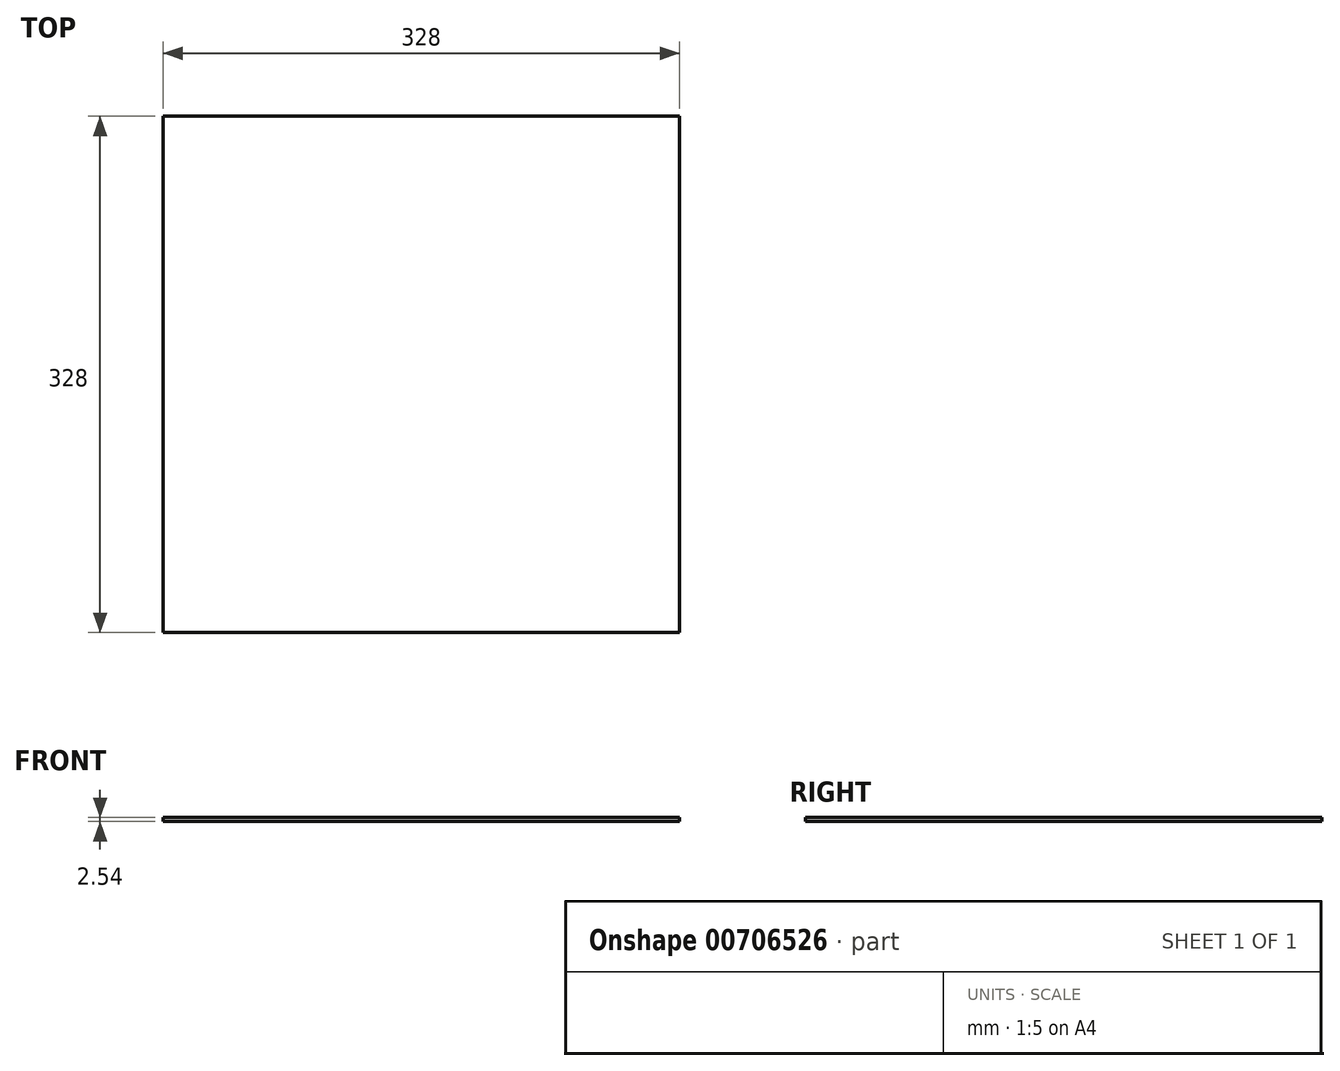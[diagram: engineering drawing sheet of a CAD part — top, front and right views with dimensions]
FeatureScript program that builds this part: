
annotation { "Feature Type Name" : "Feature", "Feature Type Description" : "" }
export const myFeature = defineFeature(function(context is Context, id is Id, definition is map)
    precondition{}
    {
        {
            var Q0;
            Q0=qCreatedBy(makeId("Top.planeOp"),FACE);
            var sketch = newSketch(context, id + "F0", { "sketchPlane" : qUnion([Q0])});
            skLineSegment(sketch, "E0.bottom", {"start": v(0, 0) * mm, "end": v(-328, 0) * mm});
            skLineSegment(sketch, "E0.top", {"start": v(0, -328) * mm, "end": v(-328, -328) * mm});
            skLineSegment(sketch, "E0.left", {"start": v(0, 0) * mm, "end": v(0, -328) * mm});
            skLineSegment(sketch, "E0.right", {"start": v(-328, 0) * mm, "end": v(-328, -328) * mm});
            skSolve(sketch);
        }
        {
            var Q0;
            Q0 = qSketchRegion(id + "F0", true);
            extrude(context, id + "F1", {"entities" : qUnion([Q0]), "depth" : 2.54 * mm, "offsetDistance" : 25.4 * mm});
        }
    });
